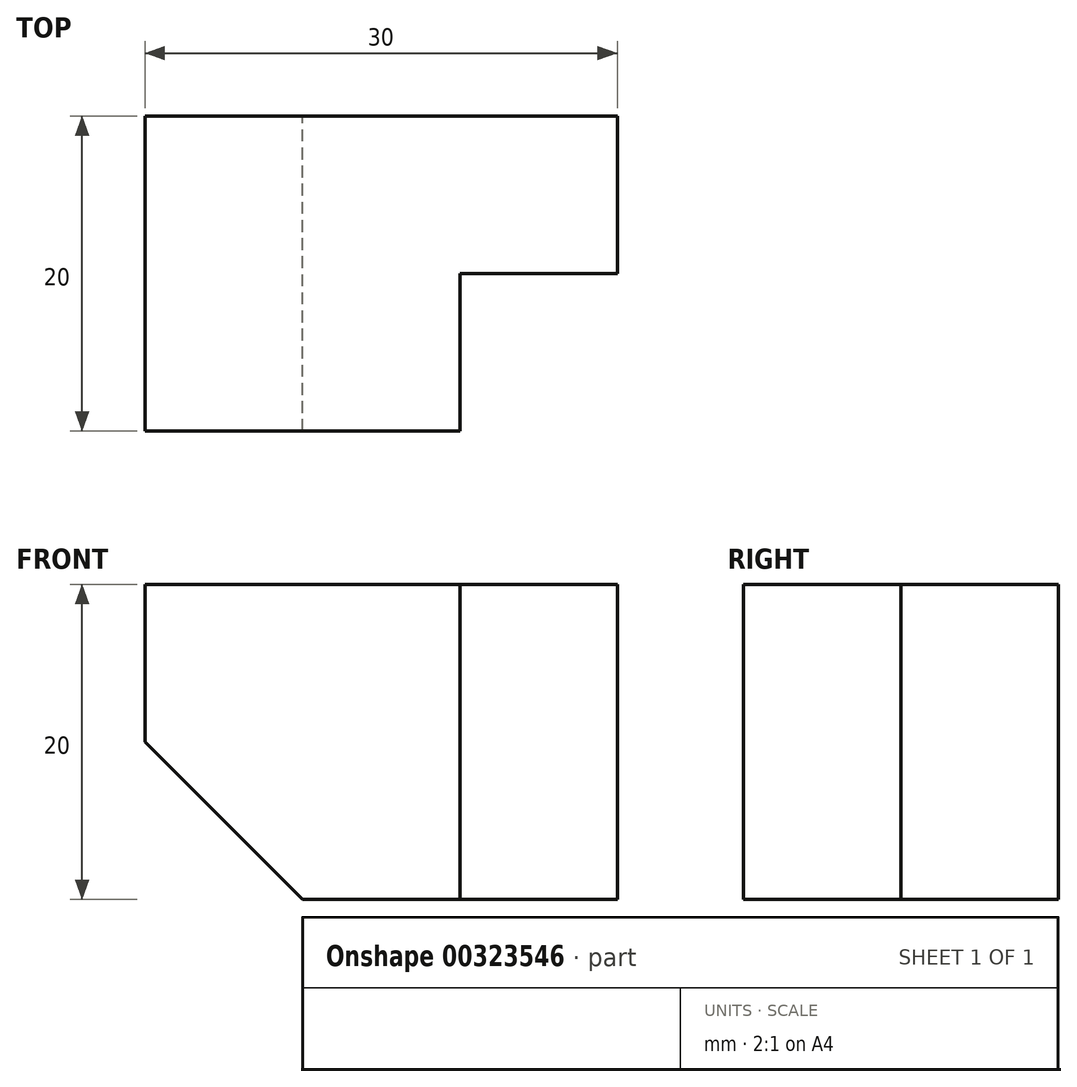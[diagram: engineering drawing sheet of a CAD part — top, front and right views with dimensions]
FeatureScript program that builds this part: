
annotation { "Feature Type Name" : "Feature", "Feature Type Description" : "" }
export const myFeature = defineFeature(function(context is Context, id is Id, definition is map)
    precondition{}
    {
        {
            var Q0;
            Q0=qCreatedBy(makeId("Front.planeOp"),FACE);
            var sketch = newSketch(context, id + "F0", { "sketchPlane" : qUnion([Q0])});
            skLineSegment(sketch, "E0", {"start": v(0, 0) * mm, "end": v(20, 0) * mm});
            skLineSegment(sketch, "E1", {"start": v(20, 0) * mm, "end": v(20, -20) * mm});
            skLineSegment(sketch, "E2", {"start": v(20, -20) * mm, "end": v(10, -20) * mm});
            skLineSegment(sketch, "E3", {"start": v(10, -20) * mm, "end": v(0, -10) * mm});
            skLineSegment(sketch, "E4", {"start": v(0, -10) * mm, "end": v(0, 0) * mm});
            skSolve(sketch);
        }
        {
            var Q0;
            Q0 = qSketchRegion(id + "F0", true);
            extrude(context, id + "F1", {"entities" : qUnion([Q0]), "depth" : 20 * mm});
        }
        {
            var Q0;
            Q0=qCreatedBy(makeId("Front.planeOp"),FACE);
            var sketch = newSketch(context, id + "F2", { "sketchPlane" : qUnion([Q0])});
            skLineSegment(sketch, "E5", {"start": v(20, 0) * mm, "end": v(20, -20) * mm});
            skLineSegment(sketch, "E6", {"start": v(20, -20) * mm, "end": v(30, -20) * mm});
            skLineSegment(sketch, "E7", {"start": v(30, -20) * mm, "end": v(30, 0) * mm});
            skLineSegment(sketch, "E8", {"start": v(30, 0) * mm, "end": v(20, 0) * mm});
            skSolve(sketch);
        }
        {
            var Q0;
            Q0 = qSketchRegion(id + "F2", true);
            extrude(context, id + "F3", {"entities" : qUnion([Q0]), "operationType" : NewBodyOperationType.ADD, "depth" : 10 * mm});
        }
    });
